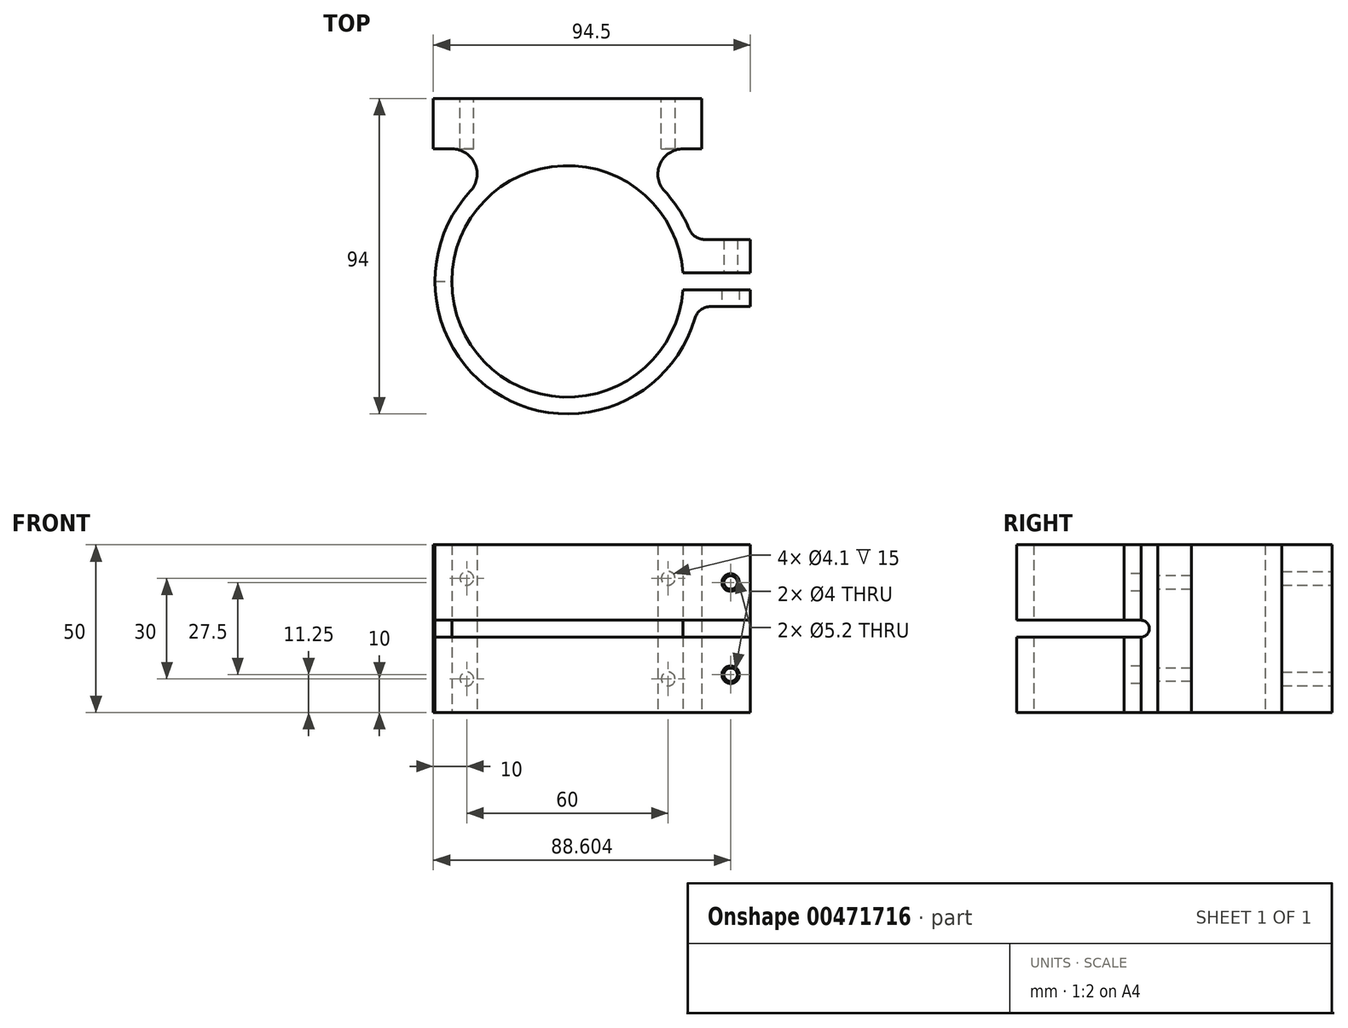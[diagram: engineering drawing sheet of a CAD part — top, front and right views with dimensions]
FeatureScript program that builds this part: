
annotation { "Feature Type Name" : "Feature", "Feature Type Description" : "" }
export const myFeature = defineFeature(function(context is Context, id is Id, definition is map)
    precondition{}
    {
        {
            var Q0;
            Q0=qCreatedBy(makeId("Top.planeOp"),FACE);
            var sketch = newSketch(context, id + "F0", { "sketchPlane" : qUnion([Q0])});
            skArc(sketch, "E0", {"start": v(34.4, 2.5) * mm, "mid": v(-34.5, 0) * mm, "end": v(34.4, -2.5) * mm});
            skArc(sketch, "E1", {"start": v(36.32, 15.53) * mm, "mid": v(33.11, 21.53) * mm, "end": v(28.93, 26.9) * mm});
            skLineSegment(sketch, "E2.bottom", {"start": v(40, 39.5) * mm, "end": v(34.42, 39.5) * mm});
            skLineSegment(sketch, "E2.top", {"start": v(40, 54.5) * mm, "end": v(-40, 54.5) * mm});
            skLineSegment(sketch, "E2.left", {"start": v(40, 39.5) * mm, "end": v(40, 54.5) * mm});
            skLineSegment(sketch, "E2.right", {"start": v(-40, 39.5) * mm, "end": v(-40, 54.5) * mm});
            skPoint(sketch, "E2.middle", {"position": v(0, 47) * mm});
            skLineSegment(sketch, "E3", {"start": v(0, 54.5) * mm, "end": v(0, 34.5) * mm});
            skLineSegment(sketch, "E4.bottom", {"start": v(54.5, -2.5) * mm, "end": v(34.4, -2.5) * mm});
            skLineSegment(sketch, "E4.top", {"start": v(54.5, 2.5) * mm, "end": v(34.4, 2.5) * mm});
            skLineSegment(sketch, "E4.right", {"start": v(14.5, -2.5) * mm, "end": v(14.5, 2.5) * mm});
            skPoint(sketch, "E4.middle", {"position": v(34.5, 0) * mm});
            skLineSegment(sketch, "E5.bottom", {"start": v(54.5, -7.5) * mm, "end": v(42.7, -7.5) * mm});
            skLineSegment(sketch, "E5.left", {"start": v(54.5, -7.5) * mm, "end": v(54.5, -2.5) * mm});
            skLineSegment(sketch, "E5.right", {"start": v(14.5, -7.5) * mm, "end": v(14.5, 7.5) * mm});
            skLineSegment(sketch, "E6.trimOffspring", {"start": v(54.5, 2.5) * mm, "end": v(54.5, 7.5) * mm});
            skPoint(sketch, "E7.visualSharp", {"position": v(38.78, 7.5) * mm});
            skPoint(sketch, "E8.visualSharp", {"position": v(38.78, -7.5) * mm});
            skArc(sketch, "E8.filletArc", {"start": v(42.7, -7.5) * mm, "mid": v(39.71, -8.5) * mm, "end": v(37.9, -11.1) * mm});
            skArc(sketch, "E9.trimOffspring", {"start": v(-28.93, 26.9) * mm, "mid": v(-19.52, -34.34) * mm, "end": v(37.9, -11.1) * mm});
            skLineSegment(sketch, "E10.trimOffspring", {"start": v(-34.42, 39.5) * mm, "end": v(-40, 39.5) * mm});
            skArc(sketch, "E11.filletArc", {"start": v(-28.93, 26.9) * mm, "mid": v(-27.55, 35) * mm, "end": v(-34.42, 39.5) * mm});
            skArc(sketch, "E12.filletArc", {"start": v(34.42, 39.5) * mm, "mid": v(27.55, 35) * mm, "end": v(28.93, 26.9) * mm});
            skLineSegment(sketch, "E13.top", {"start": v(54.5, 12.5) * mm, "end": v(40.91, 12.5) * mm});
            skLineSegment(sketch, "E13.left", {"start": v(54.5, 7.5) * mm, "end": v(54.5, 12.5) * mm});
            skPoint(sketch, "E14.visualSharp", {"position": v(37.47, 12.5) * mm});
            skArc(sketch, "E14.filletArc", {"start": v(36.32, 15.53) * mm, "mid": v(38.16, 13.33) * mm, "end": v(40.91, 12.5) * mm});
            skSolve(sketch);
        }
        {
            var Q0;
            {var subQ3=sQuery(id+"F0.wireOp",EDGE,"E2.right");Q0=makeQuery(id+"F0.imprint","IMPRINT",FACE,{"disambiguationData":[TD([[makeQuery(id+"F0.imprint","IMPRINT",EDGE,{"derivedFrom":subQ3}),-1.0]])]});}
            var Q1;
            Q1=makeQuery(id+"F0.imprint","IMPRINT",FACE,{"disambiguationData":[TD([[makeQuery(id+"F0.imprint","IMPRINT",EDGE,{"derivedFrom":sQuery(id+"F0.wireOp",EDGE,"E1")}),1.0]])]});
            extrude(context, id + "F1", {"entities" : qUnion([Q0, Q1]), "depth" : 50 * mm});
        }
        {
            var Q0;
            Q0=makeQuery(id+"F1.opExtrude","SWEPT_FACE",FACE,{"disambiguationData":[OSD([sQuery(id+"F0.wireOp",EDGE,"E2.top")])]});
            var sketch = newSketch(context, id + "F2", { "sketchPlane" : qUnion([Q0])});
            skLineSegment(sketch, "E15", {"start": v(-40, 10) * mm, "end": v(40, 10) * mm, "construction": true});
            skLineSegment(sketch, "E16", {"start": v(-40, 40) * mm, "end": v(40, 40) * mm, "construction": true});
            skCircle(sketch, "E17", {"center": v(-30, 10) * mm, "radius": 2.05 * mm});
            skCircle(sketch, "E18", {"center": v(-30, 40) * mm, "radius": 2.05 * mm});
            skCircle(sketch, "E19", {"center": v(30, 40) * mm, "radius": 2.05 * mm});
            skCircle(sketch, "E20", {"center": v(30, 10) * mm, "radius": 2.05 * mm});
            skSolve(sketch);
        }
        {
            var Q0;
            Q0=qSketchRegion(id+"F2",true);
            extrude(context, id + "F3", {"entities" : qUnion([Q0]), "operationType" : NewBodyOperationType.REMOVE, "oppositeDirection" : true, "depth" : 15 * mm});
        }
        {
            var Q0;
            Q0=qCreatedBy(makeId("Front.planeOp"),FACE);
            var sketch = newSketch(context, id + "F4", { "sketchPlane" : qUnion([Q0])});
            skLineSegment(sketch, "E21", {"start": v(0, 25) * mm, "end": v(57.85, 25) * mm});
            skArc(sketch, "E22.0.startCap", {"start": v(0, 22.5) * mm, "mid": v(-2.5, 25) * mm, "end": v(0, 27.5) * mm});
            skArc(sketch, "E22.0.endCap", {"start": v(57.85, 27.5) * mm, "mid": v(60.35, 25) * mm, "end": v(57.85, 22.5) * mm});
            skLineSegment(sketch, "E22.0.left", {"start": v(0, 27.5) * mm, "end": v(57.85, 27.5) * mm});
            skLineSegment(sketch, "E22.0.right", {"start": v(0, 22.5) * mm, "end": v(57.85, 22.5) * mm});
            skSolve(sketch);
        }
        {
            var Q0;
            {var subQ2=sQuery(id+"F0.wireOp",EDGE,"E5.bottom");Q0=makeQuery(id+"FSlxkKbNy0vXjha_1.boolean.opBoolean","SPLIT",FACE,{"disambiguationData":[TD([makeQuery(id+"FSlxkKbNy0vXjha_1.opExtrude","SWEPT_FACE",FACE,{"disambiguationData":[OSD([sQuery(id+"F4.wireOp",EDGE,"E22.0.left")])]})])],"derivedFrom":makeQuery(id+"F1.opExtrude","SWEPT_FACE",FACE,{"disambiguationData":[OSD([subQ2])]})});}
            var sketch = newSketch(context, id + "F5", { "sketchPlane" : qUnion([Q0])});
            skLineSegment(sketch, "E23", {"start": v(48.6, 50) * mm, "end": v(48.6, 0) * mm, "construction": true});
            skLineSegment(sketch, "E24", {"start": v(54.5, 11.25) * mm, "end": v(42.7, 11.25) * mm, "construction": true});
            skCircle(sketch, "E25", {"center": v(48.6, 38.75) * mm, "radius": 2.6 * mm});
            skCircle(sketch, "E26", {"center": v(48.6, 11.25) * mm, "radius": 2.6 * mm});
            skCircle(sketch, "E27", {"center": v(48.6, 38.75) * mm, "radius": 2 * mm});
            skCircle(sketch, "E28", {"center": v(48.6, 11.25) * mm, "radius": 2 * mm});
            skSolve(sketch);
        }
        {
            var Q0;
            Q0=makeQuery(id+"F5.imprint","IMPRINT",FACE,{"disambiguationData":[TD([[makeQuery(id+"F5.imprint","IMPRINT",EDGE,{"derivedFrom":sQuery(id+"F5.wireOp",EDGE,"E28")}),1.0]])]});
            var Q1;
            Q1=makeQuery(id+"F5.imprint","IMPRINT",FACE,{"disambiguationData":[TD([[makeQuery(id+"F5.imprint","IMPRINT",EDGE,{"derivedFrom":sQuery(id+"F5.wireOp",EDGE,"E27")}),1.0]])]});
            extrude(context, id + "F6", {"entities" : qUnion([Q0, Q1]), "operationType" : NewBodyOperationType.REMOVE, "endBound" : BoundingType.THROUGH_ALL, "oppositeDirection" : true, "depth" : 25 * mm});
        }
        {
            var Q0;
            Q0=makeQuery(id+"F5.imprint","IMPRINT",FACE,{"disambiguationData":[TD([[makeQuery(id+"F5.imprint","IMPRINT",EDGE,{"derivedFrom":sQuery(id+"F5.wireOp",EDGE,"E26")}),1.0]])]});
            var Q1;
            Q1=makeQuery(id+"F5.imprint","IMPRINT",FACE,{"disambiguationData":[TD([[makeQuery(id+"F5.imprint","IMPRINT",EDGE,{"derivedFrom":sQuery(id+"F5.wireOp",EDGE,"E25")}),1.0]])]});
            var Q2;
            {var subQ2=sQuery(id+"F0.wireOp",EDGE,"E4.bottom");Q2=makeQuery(id+"FSlxkKbNy0vXjha_1.boolean.opBoolean","SPLIT",FACE,{"disambiguationData":[TD([makeQuery(id+"FSlxkKbNy0vXjha_1.opExtrude","SWEPT_FACE",FACE,{"disambiguationData":[OSD([sQuery(id+"F4.wireOp",EDGE,"E22.0.right")])]})])],"derivedFrom":makeQuery(id+"F1.opExtrude","SWEPT_FACE",FACE,{"disambiguationData":[OSD([subQ2])]})});}
            extrude(context, id + "F7", {"entities" : qUnion([Q0, Q1]), "operationType" : NewBodyOperationType.REMOVE, "endBound" : BoundingType.UP_TO_SURFACE, "oppositeDirection" : true, "endBoundEntityFace" : qUnion([Q2]), "depth" : 25 * mm});
        }
        {
            var Q0;
            Q0=qCreatedBy(makeId("Right.planeOp"),FACE);
            var sketch = newSketch(context, id + "F8", { "sketchPlane" : qUnion([Q0])});
            skLineSegment(sketch, "E29", {"start": v(-2.5, 25) * mm, "end": v(-48.95, 25) * mm});
            skArc(sketch, "E30.0.startCap", {"start": v(-2.5, 27.5) * mm, "mid": v(0, 25) * mm, "end": v(-2.5, 22.5) * mm});
            skArc(sketch, "E30.0.endCap", {"start": v(-48.95, 22.5) * mm, "mid": v(-51.45, 25) * mm, "end": v(-48.95, 27.5) * mm});
            skLineSegment(sketch, "E30.0.left", {"start": v(-2.5, 22.5) * mm, "end": v(-48.95, 22.5) * mm});
            skLineSegment(sketch, "E30.0.right", {"start": v(-2.5, 27.5) * mm, "end": v(-48.95, 27.5) * mm});
            skSolve(sketch);
        }
        {
            var Q0;
            Q0=qSketchRegion(id+"F8",true);
            extrude(context, id + "F9", {"entities" : qUnion([Q0]), "operationType" : NewBodyOperationType.REMOVE, "endBound" : BoundingType.SYMMETRIC, "oppositeDirection" : true, "depth" : 200 * mm});
        }
    });
